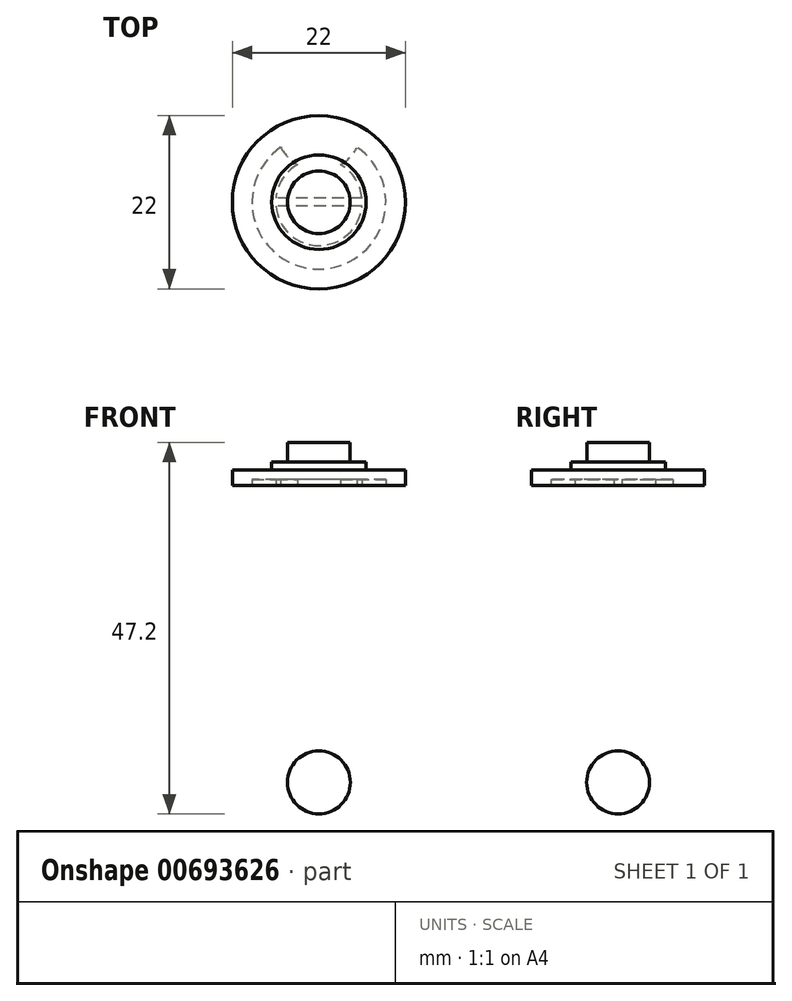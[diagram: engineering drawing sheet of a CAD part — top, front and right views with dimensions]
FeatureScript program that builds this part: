
annotation { "Feature Type Name" : "Feature", "Feature Type Description" : "" }
export const myFeature = defineFeature(function(context is Context, id is Id, definition is map)
    precondition{}
    {
        {
            var Q0;
            Q0=qCreatedBy(makeId("Top.planeOp"),FACE);
            var sketch = newSketch(context, id + "F0", { "sketchPlane" : qUnion([Q0])});
            skCircle(sketch, "E0", {"center": v(0, 0) * mm, "radius": 11 * mm});
            skSolve(sketch);
        }
        {
            var Q0;
            Q0=makeQuery(id+"F0.imprint","IMPRINT",FACE,{"disambiguationData":[TD([[makeQuery(id+"F0.imprint","IMPRINT",EDGE,{"derivedFrom":sQuery(id+"F0.wireOp",EDGE,"E0")}),1.0]])]});
            extrude(context, id + "F1", {"entities" : qUnion([Q0]), "depth" : 2 * mm, "offsetDistance" : 25 * mm});
        }
        {
            var Q0;
            Q0=makeQuery(id+"F1.opExtrude","CAP_FACE",FACE,{"disambiguationData":[OSD([sQuery(id+"F0.wireOp",EDGE,"E0")])],"isStart":false});
            var sketch = newSketch(context, id + "F2", { "sketchPlane" : qUnion([Q0])});
            skCircle(sketch, "E1", {"center": v(0, 0) * mm, "radius": 6 * mm});
            skSolve(sketch);
        }
        {
            var Q0;
            Q0 = qSketchRegion(id + "F2", true);
            extrude(context, id + "F3", {"entities" : qUnion([Q0]), "operationType" : NewBodyOperationType.ADD, "depth" : 1 * mm, "offsetDistance" : 25 * mm});
        }
        {
            var Q0;
            Q0=makeQuery(id+"F3.opExtrude","CAP_FACE",FACE,{"disambiguationData":[OSD([sQuery(id+"F2.wireOp",EDGE,"E1")])],"isStart":false});
            var sketch = newSketch(context, id + "F4", { "sketchPlane" : qUnion([Q0])});
            skCircle(sketch, "E2", {"center": v(0, 0) * mm, "radius": 3.98 * mm});
            skSolve(sketch);
        }
        {
            var Q0;
            Q0 = qSketchRegion(id + "F4", true);
            extrude(context, id + "F5", {"entities" : qUnion([Q0]), "operationType" : NewBodyOperationType.ADD, "depth" : 2.5 * mm, "offsetDistance" : 25 * mm});
        }
        {
            var Q0;
            Q0=makeQuery(id+"F1.opExtrude","CAP_FACE",FACE,{"disambiguationData":[OSD([sQuery(id+"F0.wireOp",EDGE,"E0")])],"isStart":true});
            var sketch = newSketch(context, id + "F6", { "sketchPlane" : qUnion([Q0])});
            skArc(sketch, "E3", {"start": v(5.48, 0.5) * mm, "mid": v(0, 5.5) * mm, "end": v(-5.48, 0.5) * mm});
            skArc(sketch, "E4.0", {"start": v(4.87, -6.97) * mm, "mid": v(-0.01, 8.5) * mm, "end": v(-4.85, -6.98) * mm});
            skLineSegment(sketch, "E5", {"start": v(5.5, 0) * mm, "end": v(-5.5, 0) * mm, "construction": true});
            skLineSegment(sketch, "E6.0", {"start": v(5.5, 0.5) * mm, "end": v(-5.5, 0.5) * mm});
            skLineSegment(sketch, "E7.0", {"start": v(5.5, -0.5) * mm, "end": v(-5.5, -0.5) * mm});
            skArc(sketch, "E8.trimOffspring", {"start": v(-5.48, -0.5) * mm, "mid": v(-4.63, -2.97) * mm, "end": v(-2.73, -4.77) * mm});
            skLineSegment(sketch, "E9", {"start": v(-5.48, -0.5) * mm, "end": v(-5.48, -9.54) * mm, "construction": true});
            skLineSegment(sketch, "E10", {"start": v(5.5, -0.5) * mm, "end": v(5.5, -9.53) * mm, "construction": true});
            skArc(sketch, "E11", {"start": v(4.87, -6.97) * mm, "mid": v(3.96, -5.72) * mm, "end": v(2.75, -4.77) * mm});
            skArc(sketch, "E12.trimOffspring", {"start": v(-2.73, -4.77) * mm, "mid": v(-3.95, -5.73) * mm, "end": v(-4.85, -6.98) * mm});
            skArc(sketch, "E13.trimOffspring", {"start": v(-5.48, -9.51) * mm, "mid": v(-5.48, -9.53) * mm, "end": v(-5.48, -9.54) * mm});
            skArc(sketch, "E14.trimOffspring", {"start": v(2.75, -4.77) * mm, "mid": v(4.63, -2.97) * mm, "end": v(5.48, -0.5) * mm});
            skSolve(sketch);
        }
        {
            var Q0;
            Q0 = qSketchRegion(id + "F6", true);
            extrude(context, id + "F7", {"entities" : qUnion([Q0]), "operationType" : NewBodyOperationType.REMOVE, "oppositeDirection" : true, "depth" : 0.75 * mm, "offsetDistance" : 25 * mm});
        }
        {
            var Q0;
            Q0=qCreatedBy(makeId("Front.planeOp"),FACE);
            var sketch = newSketch(context, id + "F8", { "sketchPlane" : qUnion([Q0])});
            skLineSegment(sketch, "E15", {"start": v(0, -41.7) * mm, "end": v(0, -33.7) * mm});
            skArc(sketch, "E16", {"start": v(0, -41.7) * mm, "mid": v(4, -37.7) * mm, "end": v(0, -33.7) * mm});
            skSolve(sketch);
        }
        {
            var Q0;
            Q0 = qSketchRegion(id + "F8", true);
            var Q1;
            Q1=sQuery(id+"F8.wireOp",EDGE,"E15");
            revolve(context, id + "F9", {"surfaceOperationType" : NewSurfaceOperationType.NEW, "entities" : qUnion([Q0]), "axis" : qUnion([Q1]), "revolveType" : RevolveType.FULL});
        }
    });
